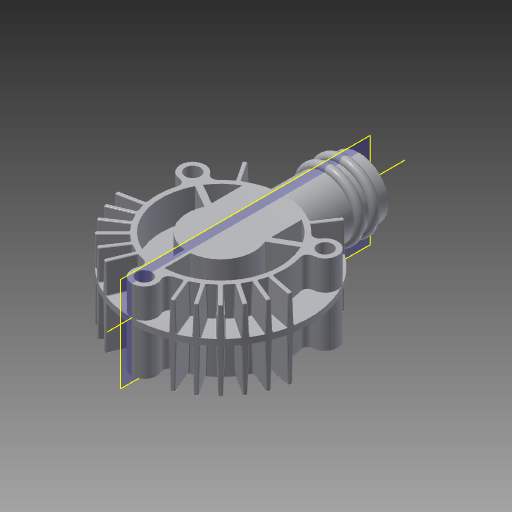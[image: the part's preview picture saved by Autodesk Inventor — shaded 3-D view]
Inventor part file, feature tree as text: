
AUTODESK INVENTOR PART (.ipt)
format: ipt  version: 2017.1 (Build 211199000, 199)  size: 2,468,864 bytes
history: native  units: in
note: dims shown in document units (in); Inventor stores cm internally (conversion verified against a paired STEP export)
features: sketch x24, extrude x21, pattern_circular x9, plane x4, draft x4, mirror x3, fillet x2, hole x2, revolve x2, other x1, thread x1
ambient origin geometry x8: Origin, YZ Plane, XZ Plane, XY Plane, X Axis, Y Axis, Z Axis, Center Point
bodies: Solid1 (feature_tree)
feature tree (73):
  extrude  "Extrusion1"  Depth=0.05in TaperAngle=0.0deg
  extrude  "Extrusion2"  Depth=1.08in
  extrude  "Extrusion3"  Depth=0.5in
  pattern_circular  "Circular Pattern1"  Count=3 Angle=360.0deg
  plane  "Work Plane2"
  extrude  "Extrusion17"  Depth=0.25in TaperAngle=0.0deg
  extrude  "Extrusion20"  Depth=0.25in
  draft  "FaceDraft5"
  draft  "FaceDraft6"
  fillet  "Fillet6"  Radius=0.125in
  pattern_circular  "Circular Pattern7"  Count=3 Angle=360.0deg
  extrude  "Extrusion21"  Depth=0.25in TaperAngle=360.0deg
  pattern_circular  "Circular Pattern8"  [2 undecoded]
  extrude  "Extrusion22"  Depth=0.25in
  draft  "FaceDraft7"
  draft  "FaceDraft8"
  fillet  "Fillet7"  Radius=0.125in
  pattern_circular  "Circular Pattern9"  [2 undecoded]
  extrude  "Extrusion23"  Depth=0.25in
  pattern_circular  "Circular Pattern10"  [2 undecoded]
  hole  "Hole1"  [1 undecoded]
  pattern_circular  "Circular Pattern11"  [2 undecoded]
  extrude  "Extrusion24"  Depth=0.25in
  plane  "Work Plane5"
  extrude  "Extrusion25"  Depth=0.25in TaperAngle=0.0deg
  hole  "Hole2"  [1 undecoded]
  other  "Work Axis1"
  revolve  "Revolution2"  [1 undecoded]
  pattern_circular  "Circular Pattern2"  [2 undecoded]
  extrude  "Extrusion5"  Depth=0.25in TaperAngle=360.0deg
  extrude  "Extrusion6"  Depth=0.25in
  mirror  "Mirror1"
  mirror  "Mirror2"
  extrude  "Extrusion7"  Depth=0.25in
  extrude  "Extrusion8"  Depth=0.25in TaperAngle=0.0deg
  extrude  "Extrusion9"  Depth=0.25in TaperAngle=360.0deg
  pattern_circular  "Circular Pattern3"  [2 undecoded]
  mirror  "Mirror3"
  extrude  "Extrusion10"  Depth=0.25in
  pattern_circular  "Circular Pattern4"  [2 undecoded]
  extrude  "Extrusion11"  Depth=0.25in
  plane  "Work Plane1"
  extrude  "Extrusion12"  Depth=0.25in TaperAngle=360.0deg
  extrude  "Extrusion13"  Depth=0.25in TaperAngle=0.0deg
  revolve  "Revolution1"  Angle=360.0deg
  extrude  "Extrusion14"  Depth=0.25in
  extrude  "Extrusion16"  Depth=0.25in TaperAngle=360.0deg
  thread  "Thread1"  [1 undecoded]
  sketch  "Sketch1"  dims[d0=1.5in d1=0.05in d2=0.0in]
  sketch  "Sketch2"  dims[d3=1.0in d4=1.08in]
  sketch  "Sketch3"  dims[d5=0.5625in d6=0.5in]
  sketch  "Sketch5"  dims[d7=0.25in d8=0.0in]
  sketch  "Sketch6"  dims[d9=0.05in]
  sketch  "Sketch7"  dims[d10=0.25in d11=0.0in d12=1.1811in d13=360.0deg]
  sketch  "Sketch8"  dims[d20=11.0236in d21=360.0deg d23=0.25in d24=0.0in]
  sketch  "Sketch9"  dims[d25=0.25in d26=0.0in d27=0.5in d28=0.125in d29=0.0in]
  sketch  "Sketch10"  dims[d30=1.0in]
  sketch  "Sketch11"  dims[d31=0.25in d32=0.0in]
  sketch  "Sketch12"  dims[d35=0.25in]
  sketch  "Sketch13"  dims[d36=0.2in]
  sketch  "Sketch14"  dims[d37=0.25in d38=0.0in d39=1.1811in d40=360.0deg]
  sketch  "Sketch15"  dims[d42=0.25in d43=0.0in d44=1.1811in d45=360.0deg]
  sketch  "Sketch17"  dims[d47=0.25in d48=0.0in]
  sketch  "Sketch18"  dims[d49=0.5in]
  sketch  "Sketch20"  dims[d50=0.0625in d51=0.625in d52=0.0in d53=0.0in]
  sketch  "Sketch21"  dims[d54=0.25in d55=0.0in]
  sketch  "Sketch22"  dims[d57=0.1in]
  sketch  "Sketch23"  dims[d58=0.1in]
  sketch  "Sketch24"  dims[d59=0.05in]
  plane  "Work Plane4"
  sketch  "Sketch26"  dims[d60=0.25in]
  sketch  "Sketch27"  dims[d61=0.5in]
  sketch  "Sketch28"  dims[d62=90.0deg d63=0.75in d64=0.0in d67=0.2in d68=0.125in d69=0.0in d70=1.0in d71=0.0in d72=0.25in d76=0.375in d77=0.0in d106=22.5deg d107=0.025in d108=0.025in d109=0.25in d110=0.0in d111=0.0137in d112=0.0137in d113=0.01in d114=12.5984in d115=360.0deg d117=0.1in d118=0.1in d119=0.25in d120=0.0in d121=1.1811in d122=360.0deg d124=0.25in d125=0.0in d126=0.0103in d127=0.0103in d128=0.01in d129=12.5984in d130=360.0deg d132=0.25in d133=0.0in d134=1.1811in d135=360.0deg d137=1.0in d138=1.0in d139=0.129in d140=0.75in d141=0.219in d142=0.112in d143=0.5635in d144=1.0in d145=0.8108in d146=1.1811in d147=360.0deg d149=0.125in d150=0.0in d152=-0.625in d153=0.5in d154=0.5625in d155=0.0in d156=0.313in d157=0.236in d158=0.0246in d159=0.329in d160=0.219in d161=0.112in d162=0.5635in d163=0.25in d164=0.8108in d165=0.125in d166=0.25in d167=90.0deg]
note: 18 required parameter values undecoded (feature->parameter linkage not recoverable at this tier; creation-order binding heuristic only, values carry confidence <= 0.55)